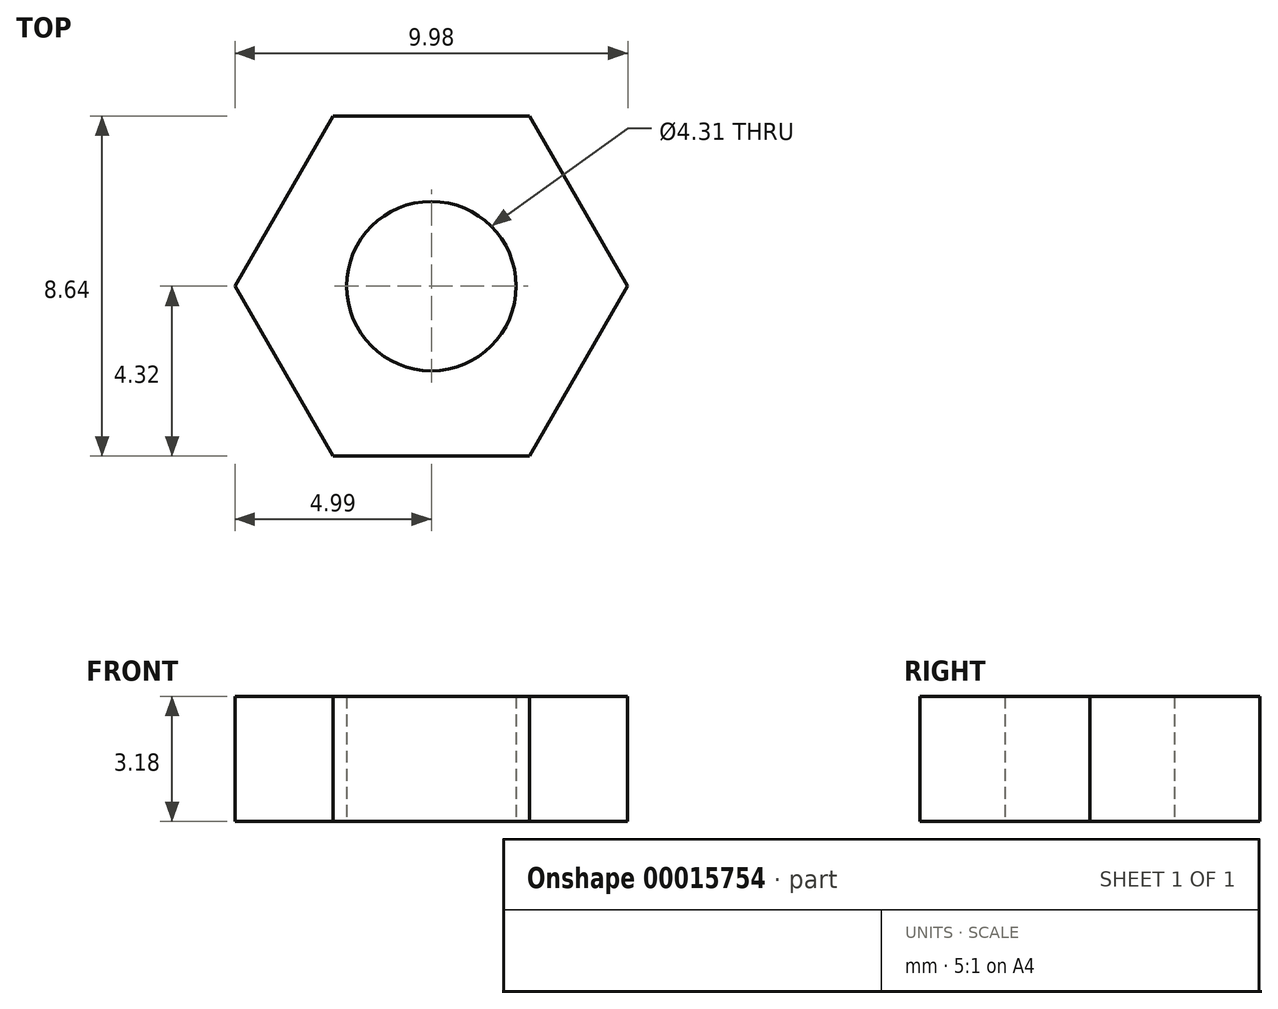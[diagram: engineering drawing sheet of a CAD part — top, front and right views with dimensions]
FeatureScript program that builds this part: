
annotation { "Feature Type Name" : "Feature", "Feature Type Description" : "" }
export const myFeature = defineFeature(function(context is Context, id is Id, definition is map)
    precondition{}
    {
        {
            var Q0;
            Q0=qCreatedBy(makeId("Top.planeOp"),FACE);
            var sketch = newSketch(context, id + "F0", { "sketchPlane" : qUnion([Q0])});
            skCircle(sketch, "E0", {"center": v(0, 0) * mm, "radius": 2.15 * mm});
            skCircle(sketch, "E1.cCircle", {"center": v(0, 0) * mm, "radius": 4.32 * mm, "construction": true});
            skLineSegment(sketch, "E1.0", {"start": v(2.5, -4.32) * mm, "end": v(-2.5, -4.32) * mm});
            skLineSegment(sketch, "E1.1", {"start": v(-2.5, -4.32) * mm, "end": v(-4.99, 0) * mm});
            skLineSegment(sketch, "E1.2", {"start": v(-4.99, 0) * mm, "end": v(-2.5, 4.32) * mm});
            skLineSegment(sketch, "E1.3", {"start": v(-2.5, 4.32) * mm, "end": v(2.5, 4.32) * mm});
            skLineSegment(sketch, "E1.4", {"start": v(2.5, 4.32) * mm, "end": v(4.99, 0) * mm});
            skLineSegment(sketch, "E1.5", {"start": v(4.99, 0) * mm, "end": v(2.5, -4.32) * mm});
            skPoint(sketch, "E1.0.midPoint", {"position": v(0, -4.32) * mm});
            skSolve(sketch);
        }
        {
            var Q0;
            Q0 = qSketchRegion(id + "F0", true);
            extrude(context, id + "F1", {"entities" : qUnion([Q0]), "depth" : 3.17 * mm});
        }
    });
